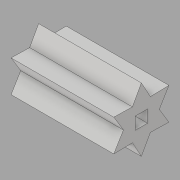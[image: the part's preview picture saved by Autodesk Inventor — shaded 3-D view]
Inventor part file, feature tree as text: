
AUTODESK INVENTOR PART (.ipt)
format: ipt  version: 2017 (Build 210142000, 142)  size: 129,536 bytes
history: native  units: in
note: dims shown in document units (in); Inventor stores cm internally (conversion verified against a paired STEP export)
features: extrude x2, sketch x2, projected_geometry x1
ambient origin geometry x8: Origin, YZ Plane, XZ Plane, XY Plane, X Axis, Y Axis, Z Axis, Center Point
bodies: Solid1 (feature_tree)
feature tree (5):
  extrude  "Extrusion1"  Depth=0.12in
  extrude  "Extrusion2"  Depth=1.0in TaperAngle=360.0deg
  sketch  "Sketch1"  dims[d0=0.12in d1=0.05in]
  sketch  "Sketch2"  dims[d2=0.2in d3=2.3622in d5=360.0deg d7=1.0in d8=0.0in d9=1.0in d10=0.0in]
  projected_geometry  "Projected Loop1"
